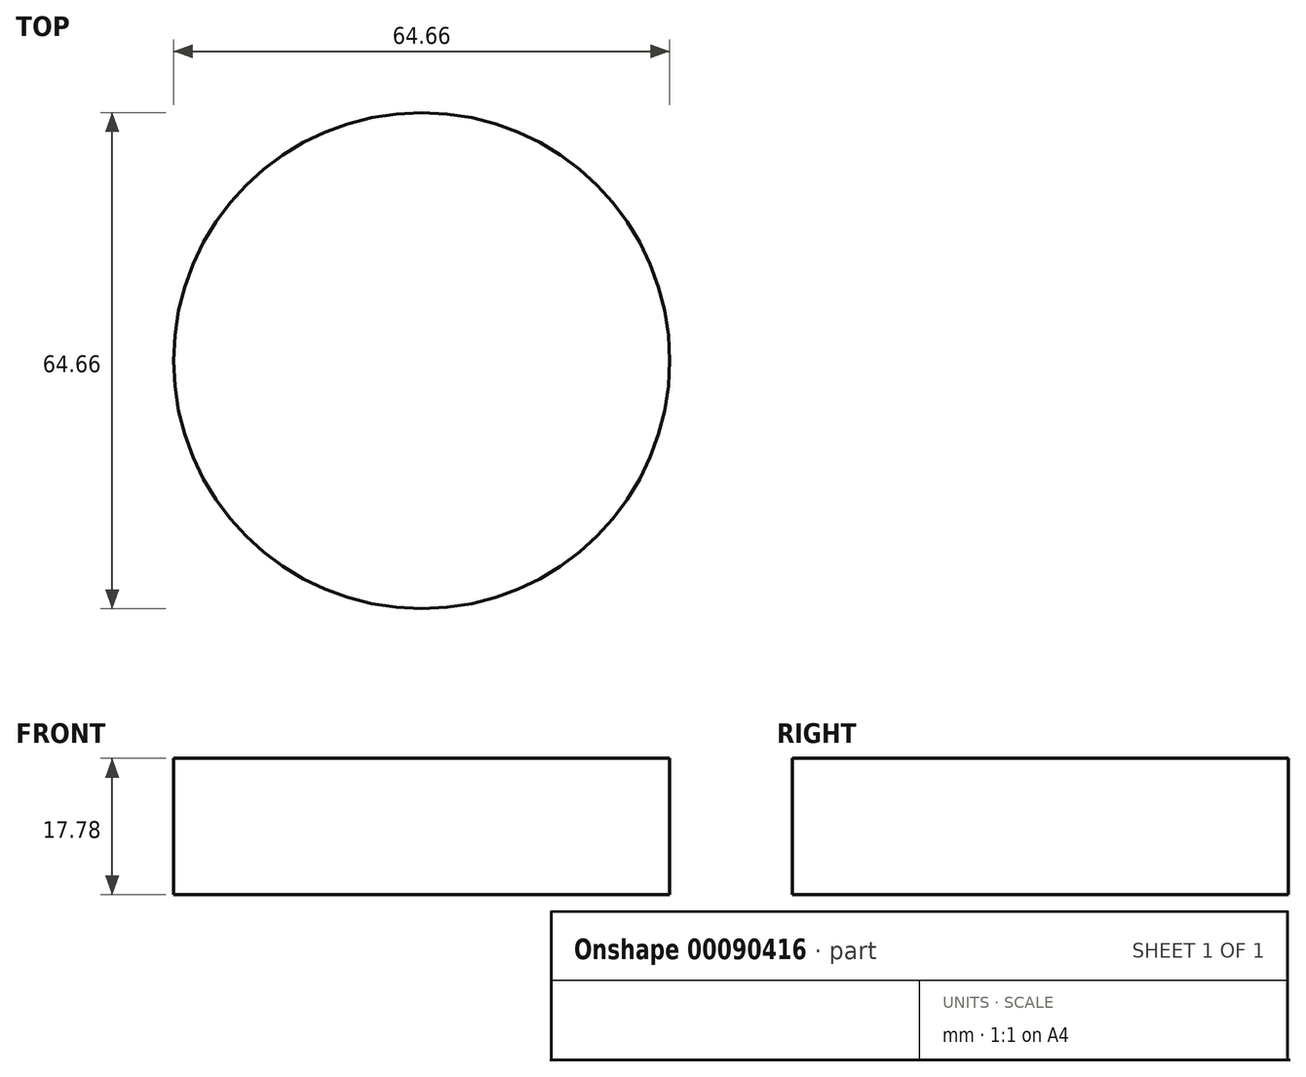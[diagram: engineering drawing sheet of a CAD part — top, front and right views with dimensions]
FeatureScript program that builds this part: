
annotation { "Feature Type Name" : "Feature", "Feature Type Description" : "" }
export const myFeature = defineFeature(function(context is Context, id is Id, definition is map)
    precondition{}
    {
        {
            var Q0;
            Q0=qCreatedBy(makeId("Top.planeOp"),FACE);
            var sketch = newSketch(context, id + "F0", { "sketchPlane" : qUnion([Q0])});
            skLineSegment(sketch, "E0.bottom", {"start": v(-17.32, 19.66) * mm, "end": v(15.7, 19.66) * mm});
            skLineSegment(sketch, "E0.top", {"start": v(-17.32, -13.36) * mm, "end": v(15.7, -13.36) * mm});
            skLineSegment(sketch, "E0.left", {"start": v(-17.32, 19.66) * mm, "end": v(-17.32, -13.36) * mm});
            skLineSegment(sketch, "E0.right", {"start": v(15.7, 19.66) * mm, "end": v(15.7, -13.36) * mm});
            skLineSegment(sketch, "E1.bottom", {"start": v(-4.62, -13.36) * mm, "end": v(3, -13.36) * mm});
            skLineSegment(sketch, "E1.top", {"start": v(-4.62, -8.28) * mm, "end": v(3, -8.28) * mm});
            skLineSegment(sketch, "E1.left", {"start": v(-4.62, -13.36) * mm, "end": v(-4.62, -8.28) * mm});
            skLineSegment(sketch, "E1.right", {"start": v(3, -13.36) * mm, "end": v(3, -8.28) * mm});
            skSolve(sketch);
        }
        {
            var Q0;
            Q0=makeQuery(id+"F0.imprint","IMPRINT",FACE,{"disambiguationData":[TD([[makeQuery(id+"F0.imprint","IMPRINT",EDGE,{"derivedFrom":sQuery(id+"F0.wireOp",EDGE,"E0.bottom")}),-1.0]])]});
            extrude(context, id + "F1", {"entities" : qUnion([Q0]), "depth" : 5.08 * mm});
        }
        {
            var Q0;
            Q0=makeQuery(id+"F1.opExtrude","CAP_FACE",FACE,{"disambiguationData":[OSD([sQuery(id+"F0.wireOp",EDGE,"E0.bottom"),sQuery(id+"F0.wireOp",EDGE,"E0.top"),sQuery(id+"F0.wireOp",EDGE,"E0.left"),sQuery(id+"F0.wireOp",EDGE,"E0.right"),sQuery(id+"F0.wireOp",EDGE,"E1.top"),sQuery(id+"F0.wireOp",EDGE,"E1.left"),sQuery(id+"F0.wireOp",EDGE,"E1.right")])],"isStart":false});
            var sketch = newSketch(context, id + "F2", { "sketchPlane" : qUnion([Q0])});
            skLineSegment(sketch, "E2.bottom", {"start": v(-17.32, 19.66) * mm, "end": v(22.05, 19.66) * mm});
            skLineSegment(sketch, "E2.top", {"start": v(-17.32, 26) * mm, "end": v(22.05, 26) * mm});
            skLineSegment(sketch, "E2.left", {"start": v(-17.32, 19.66) * mm, "end": v(-17.32, 26) * mm});
            skLineSegment(sketch, "E2.right", {"start": v(22.05, 19.66) * mm, "end": v(22.05, 26) * mm});
            skLineSegment(sketch, "E3.bottom", {"start": v(22.05, 19.66) * mm, "end": v(15.7, 19.66) * mm});
            skLineSegment(sketch, "E3.top", {"start": v(22.05, -13.36) * mm, "end": v(15.7, -13.36) * mm});
            skLineSegment(sketch, "E3.left", {"start": v(22.05, 19.66) * mm, "end": v(22.05, -13.36) * mm});
            skLineSegment(sketch, "E3.right", {"start": v(15.7, 19.66) * mm, "end": v(15.7, -13.36) * mm});
            skLineSegment(sketch, "E4.bottom", {"start": v(22.05, -13.36) * mm, "end": v(-17.32, -13.36) * mm});
            skLineSegment(sketch, "E4.top", {"start": v(22.05, -19.71) * mm, "end": v(-17.32, -19.71) * mm});
            skLineSegment(sketch, "E4.left", {"start": v(22.05, -13.36) * mm, "end": v(22.05, -19.71) * mm});
            skLineSegment(sketch, "E4.right", {"start": v(-17.32, -13.36) * mm, "end": v(-17.32, -19.71) * mm});
            skLineSegment(sketch, "E5.bottom", {"start": v(-17.32, -19.71) * mm, "end": v(-23.67, -19.71) * mm});
            skLineSegment(sketch, "E5.top", {"start": v(-17.32, 26) * mm, "end": v(-23.67, 26) * mm});
            skLineSegment(sketch, "E5.left", {"start": v(-17.32, -19.71) * mm, "end": v(-17.32, 26) * mm});
            skLineSegment(sketch, "E5.right", {"start": v(-23.67, -19.71) * mm, "end": v(-23.67, 26) * mm});
            skSolve(sketch);
        }
        {
            var Q0;
            Q0=makeQuery(id+"F2.imprint","IMPRINT",FACE,{"disambiguationData":[TD([[makeQuery(id+"F2.imprint","IMPRINT",EDGE,{"derivedFrom":sQuery(id+"F2.wireOp",EDGE,"E3.bottom")}),1.0]])]});
            var Q1;
            {var subQ1=sQuery(id+"F2.wireOp",EDGE,"E2.bottom");Q1=makeQuery(id+"F2.imprint","IMPRINT",FACE,{"disambiguationData":[TD([[makeQuery(id+"F2.imprint","IMPRINT",EDGE,{"derivedFrom":subQ1}),1.0]])]});}
            var Q2;
            {var subQ7=sQuery(id+"F2.wireOp",EDGE,"E4.top");Q2=makeQuery(id+"F2.imprint","IMPRINT",FACE,{"disambiguationData":[TD([[makeQuery(id+"F2.imprint","IMPRINT",EDGE,{"derivedFrom":subQ7}),-1.0]])]});}
            var Q3;
            {var subQ3=sQuery(id+"F2.wireOp",EDGE,"E5.bottom");Q3=makeQuery(id+"F2.imprint","IMPRINT",FACE,{"disambiguationData":[TD([[makeQuery(id+"F2.imprint","IMPRINT",EDGE,{"derivedFrom":subQ3}),-1.0]])]});}
            extrude(context, id + "F3", {"entities" : qUnion([Q0, Q1, Q2, Q3]), "operationType" : NewBodyOperationType.ADD, "oppositeDirection" : true, "depth" : 5.08 * mm});
        }
        {
            var Q0;
            {var subQ1=sQuery(id+"F2.wireOp",EDGE,"E2.bottom");Q0=makeQuery(id+"F2.imprint","IMPRINT",FACE,{"disambiguationData":[TD([[makeQuery(id+"F2.imprint","IMPRINT",EDGE,{"derivedFrom":subQ1}),1.0]])]});}
            var Q1;
            Q1=makeQuery(id+"F2.imprint","IMPRINT",FACE,{"disambiguationData":[TD([[makeQuery(id+"F2.imprint","IMPRINT",EDGE,{"derivedFrom":sQuery(id+"F2.wireOp",EDGE,"E3.bottom")}),1.0]])]});
            var Q2;
            {var subQ7=sQuery(id+"F2.wireOp",EDGE,"E4.top");Q2=makeQuery(id+"F2.imprint","IMPRINT",FACE,{"disambiguationData":[TD([[makeQuery(id+"F2.imprint","IMPRINT",EDGE,{"derivedFrom":subQ7}),-1.0]])]});}
            var Q3;
            {var subQ3=sQuery(id+"F2.wireOp",EDGE,"E5.bottom");Q3=makeQuery(id+"F2.imprint","IMPRINT",FACE,{"disambiguationData":[TD([[makeQuery(id+"F2.imprint","IMPRINT",EDGE,{"derivedFrom":subQ3}),-1.0]])]});}
            extrude(context, id + "F4", {"entities" : qUnion([Q0, Q1, Q2, Q3]), "operationType" : NewBodyOperationType.ADD, "depth" : 12.7 * mm});
        }
        {
            var Q0;
            Q0=makeQuery(id+"F3.boolean.opBoolean","MERGE",FACE,{"derivedFrom":[makeQuery(id+"F1.opExtrude","CAP_FACE",FACE,{"disambiguationData":[OSD([sQuery(id+"F0.wireOp",EDGE,"E0.bottom"),sQuery(id+"F0.wireOp",EDGE,"E0.top"),sQuery(id+"F0.wireOp",EDGE,"E0.left"),sQuery(id+"F0.wireOp",EDGE,"E0.right"),sQuery(id+"F0.wireOp",EDGE,"E1.top"),sQuery(id+"F0.wireOp",EDGE,"E1.left"),sQuery(id+"F0.wireOp",EDGE,"E1.right")])],"isStart":false}),makeQuery(id+"F3.opExtrude","CAP_FACE",FACE,{"disambiguationData":[OSD([sQuery(id+"F2.wireOp",EDGE,"E2.bottom"),sQuery(id+"F2.wireOp",EDGE,"E2.top"),sQuery(id+"F2.wireOp",EDGE,"E2.right"),sQuery(id+"F2.wireOp",EDGE,"E3.left"),sQuery(id+"F2.wireOp",EDGE,"E3.right"),sQuery(id+"F2.wireOp",EDGE,"E4.bottom"),sQuery(id+"F2.wireOp",EDGE,"E4.top"),sQuery(id+"F2.wireOp",EDGE,"E4.left"),sQuery(id+"F2.wireOp",EDGE,"E5.bottom"),sQuery(id+"F2.wireOp",EDGE,"E5.top"),sQuery(id+"F2.wireOp",EDGE,"E5.left"),sQuery(id+"F2.wireOp",EDGE,"E5.right")])],"isStart":true})]});
            var sketch = newSketch(context, id + "F5", { "sketchPlane" : qUnion([Q0])});
            skCircle(sketch, "E6", {"center": v(-14.9, 17.24) * mm, "radius": 1.14 * mm});
            skCircle(sketch, "E7", {"center": v(13.29, 17.24) * mm, "radius": 1.14 * mm});
            skCircle(sketch, "E8", {"center": v(-14.9, -10.95) * mm, "radius": 1.14 * mm});
            skCircle(sketch, "E9", {"center": v(13.29, -10.95) * mm, "radius": 1.14 * mm});
            skSolve(sketch);
        }
        {
            var Q0;
            Q0=makeQuery(id+"F5.imprint","IMPRINT",FACE,{"disambiguationData":[TD([[makeQuery(id+"F5.imprint","IMPRINT",EDGE,{"derivedFrom":sQuery(id+"F5.wireOp",EDGE,"E7")}),1.0]])]});
            var Q1;
            Q1=makeQuery(id+"F5.imprint","IMPRINT",FACE,{"disambiguationData":[TD([[makeQuery(id+"F5.imprint","IMPRINT",EDGE,{"derivedFrom":sQuery(id+"F5.wireOp",EDGE,"E8")}),1.0]])]});
            var Q2;
            Q2=makeQuery(id+"F5.imprint","IMPRINT",FACE,{"disambiguationData":[TD([[makeQuery(id+"F5.imprint","IMPRINT",EDGE,{"derivedFrom":sQuery(id+"F5.wireOp",EDGE,"E9")}),1.0]])]});
            var Q3;
            Q3=makeQuery(id+"F5.imprint","IMPRINT",FACE,{"disambiguationData":[TD([[makeQuery(id+"F5.imprint","IMPRINT",EDGE,{"derivedFrom":sQuery(id+"F5.wireOp",EDGE,"E6")}),1.0]])]});
            extrude(context, id + "F6", {"entities" : qUnion([Q0, Q1, Q2, Q3]), "operationType" : NewBodyOperationType.REMOVE, "oppositeDirection" : true, "depth" : 25.4 * mm});
        }
        {
            var Q0;
            Q0=makeQuery(id+"F4.opExtrude","CAP_FACE",FACE,{"disambiguationData":[OSD([sQuery(id+"F2.wireOp",EDGE,"E2.bottom"),sQuery(id+"F2.wireOp",EDGE,"E2.top"),sQuery(id+"F2.wireOp",EDGE,"E2.right"),sQuery(id+"F2.wireOp",EDGE,"E3.left"),sQuery(id+"F2.wireOp",EDGE,"E3.right"),sQuery(id+"F2.wireOp",EDGE,"E4.bottom"),sQuery(id+"F2.wireOp",EDGE,"E4.top"),sQuery(id+"F2.wireOp",EDGE,"E4.left"),sQuery(id+"F2.wireOp",EDGE,"E5.bottom"),sQuery(id+"F2.wireOp",EDGE,"E5.top"),sQuery(id+"F2.wireOp",EDGE,"E5.left"),sQuery(id+"F2.wireOp",EDGE,"E5.right")])],"isStart":false});
            var sketch = newSketch(context, id + "F7", { "sketchPlane" : qUnion([Q0])});
            skCircle(sketch, "E10", {"center": v(-0.81, 3.15) * mm, "radius": 32.33 * mm});
            skPoint(sketch, "E10.first.point", {"position": v(-23.67, 26) * mm});
            skPoint(sketch, "E10.second.point", {"position": v(22.05, -19.71) * mm});
            skPoint(sketch, "E10.third.point", {"position": v(22.05, 26) * mm});
            skSolve(sketch);
        }
        {
            var Q0;
            {var subQ1=makeQuery(id+"F4.opExtrude","CAP_EDGE",EDGE,{"disambiguationData":[OSD([sQuery(id+"F2.wireOp",EDGE,"E4.top"),sQuery(id+"F2.wireOp",EDGE,"E5.bottom")])],"isStart":false});Q0=makeQuery(id+"F7.imprint","IMPRINT",FACE,{"disambiguationData":[TD([[makeQuery(id+"F7.imprint","IMPRINT",EDGE,{"derivedFrom":subQ1}),1.0]])]});}
            var Q1;
            {var subQ1=makeQuery(id+"F4.opExtrude","CAP_EDGE",EDGE,{"disambiguationData":[OSD([sQuery(id+"F2.wireOp",EDGE,"E5.right")])],"isStart":false});Q1=makeQuery(id+"F7.imprint","IMPRINT",FACE,{"disambiguationData":[TD([[makeQuery(id+"F7.imprint","IMPRINT",EDGE,{"derivedFrom":subQ1}),1.0]])]});}
            var Q2;
            {var subQ1=makeQuery(id+"F4.opExtrude","CAP_EDGE",EDGE,{"disambiguationData":[OSD([sQuery(id+"F2.wireOp",EDGE,"E2.right"),sQuery(id+"F2.wireOp",EDGE,"E3.left"),sQuery(id+"F2.wireOp",EDGE,"E4.left")])],"isStart":false});Q2=makeQuery(id+"F7.imprint","IMPRINT",FACE,{"disambiguationData":[TD([[makeQuery(id+"F7.imprint","IMPRINT",EDGE,{"derivedFrom":subQ1}),-1.0]])]});}
            var Q3;
            {var subQ1=makeQuery(id+"F4.opExtrude","CAP_EDGE",EDGE,{"disambiguationData":[OSD([sQuery(id+"F2.wireOp",EDGE,"E2.top"),sQuery(id+"F2.wireOp",EDGE,"E5.top")])],"isStart":false});Q3=makeQuery(id+"F7.imprint","IMPRINT",FACE,{"disambiguationData":[TD([[makeQuery(id+"F7.imprint","IMPRINT",EDGE,{"derivedFrom":subQ1}),1.0]])]});}
            extrude(context, id + "F8", {"entities" : qUnion([Q0, Q1, Q2, Q3]), "operationType" : NewBodyOperationType.ADD, "oppositeDirection" : true, "depth" : 17.78 * mm});
        }
    });
